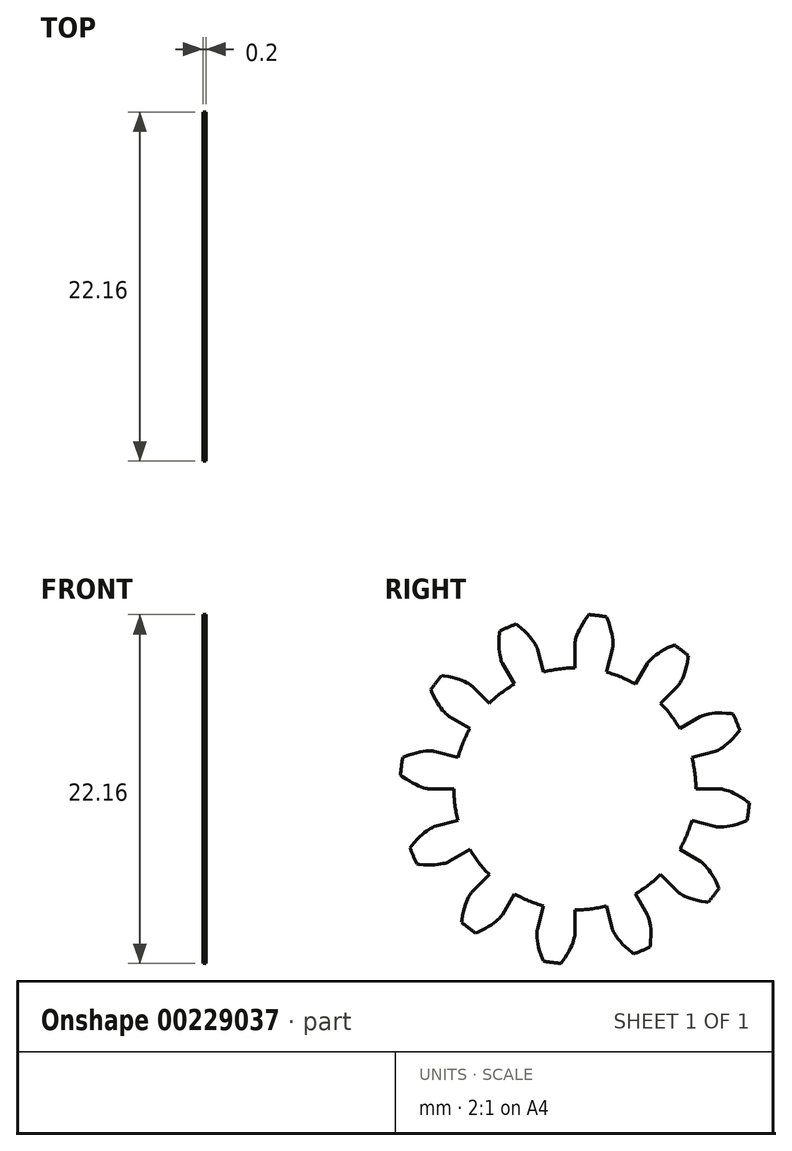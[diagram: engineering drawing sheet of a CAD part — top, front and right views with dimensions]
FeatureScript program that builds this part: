
annotation { "Feature Type Name" : "Feature", "Feature Type Description" : "" }
export const myFeature = defineFeature(function(context is Context, id is Id, definition is map)
    precondition{}
    {
        {
            assignVariable(context, id + "F0", {"name" : "GearThickness", "anyValue" : .196});
        }
        {
            var Q0;
            Q0=qCreatedBy(makeId("Right.planeOp"),FACE);
            var sketch = newSketch(context, id + "F1", { "sketchPlane" : qUnion([Q0])});
            skCircle(sketch, "E0", {"center": v(0, 0) * mm, "radius": 7.69 * mm});
            skCircle(sketch, "E1", {"center": v(0, 0) * mm, "radius": 9.22 * mm, "construction": true});
            skCircle(sketch, "E2", {"center": v(0, 0) * mm, "radius": 9.53 * mm, "construction": true});
            skCircle(sketch, "E3", {"center": v(0, 0) * mm, "radius": 11.11 * mm});
            skLineSegment(sketch, "E4", {"start": v(0, 0) * mm, "end": v(-9.22, 0) * mm, "construction": true});
            skLineSegment(sketch, "E5.1.0", {"start": v(0, 0) * mm, "end": v(-9.21, 0.46) * mm, "construction": true});
            skLineSegment(sketch, "E5.2.0", {"start": v(0, 0) * mm, "end": v(-9.18, 0.92) * mm, "construction": true});
            skLineSegment(sketch, "E5.3.0", {"start": v(0, 0) * mm, "end": v(-9.12, 1.38) * mm, "construction": true});
            skLineSegment(sketch, "E5.4.0", {"start": v(0, 0) * mm, "end": v(-9.04, 1.83) * mm, "construction": true});
            skLineSegment(sketch, "E5.5.0", {"start": v(0, 0) * mm, "end": v(-8.93, 2.28) * mm, "construction": true});
            skLineSegment(sketch, "E5.6.0", {"start": v(0, 0) * mm, "end": v(-8.8, 2.73) * mm, "construction": true});
            skLineSegment(sketch, "E5.7.0", {"start": v(0, 0) * mm, "end": v(-8.66, 3.16) * mm, "construction": true});
            skLineSegment(sketch, "E5.8.0", {"start": v(0, 0) * mm, "end": v(-8.5, 3.6) * mm, "construction": true});
            skLineSegment(sketch, "E5.9.0", {"start": v(0, 0) * mm, "end": v(-8.3, 4.01) * mm, "construction": true});
            skLineSegment(sketch, "E5.10.0", {"start": v(0, 0) * mm, "end": v(-8.1, 4.42) * mm, "construction": true});
            skLineSegment(sketch, "E5.11.0", {"start": v(0, 0) * mm, "end": v(-7.86, 4.82) * mm, "construction": true});
            skLineSegment(sketch, "E5.12.0", {"start": v(0, 0) * mm, "end": v(-7.61, 5.2) * mm, "construction": true});
            skLineSegment(sketch, "E5.13.0", {"start": v(0, 0) * mm, "end": v(-7.34, 5.58) * mm, "construction": true});
            skLineSegment(sketch, "E5.14.0", {"start": v(0, 0) * mm, "end": v(-7.05, 5.94) * mm, "construction": true});
            skLineSegment(sketch, "E5.anchor2", {"start": v(0, 0) * mm, "end": v(-7.05, 5.94) * mm, "construction": true});
            skLineSegment(sketch, "E6", {"start": v(-9.21, 0.46) * mm, "end": v(-9.23, 0) * mm, "construction": true});
            skLineSegment(sketch, "E7", {"start": v(-9.18, 0.92) * mm, "end": v(-9.27, 0) * mm, "construction": true});
            skLineSegment(sketch, "E8", {"start": v(-9.12, 1.38) * mm, "end": v(-9.32, 0.01) * mm, "construction": true});
            skLineSegment(sketch, "E9", {"start": v(-8.93, 2.28) * mm, "end": v(-9.5, 0.05) * mm, "construction": true});
            skLineSegment(sketch, "E10", {"start": v(-8.8, 2.73) * mm, "end": v(-9.63, 0.08) * mm, "construction": true});
            skLineSegment(sketch, "E11", {"start": v(-8.66, 3.16) * mm, "end": v(-9.77, 0.13) * mm, "construction": true});
            skLineSegment(sketch, "E12", {"start": v(-8.5, 3.6) * mm, "end": v(-9.93, 0.2) * mm, "construction": true});
            skLineSegment(sketch, "E13", {"start": v(-8.3, 4.01) * mm, "end": v(-10.1, 0.27) * mm, "construction": true});
            skLineSegment(sketch, "E14", {"start": v(-8.1, 4.42) * mm, "end": v(-10.3, 0.37) * mm, "construction": true});
            skLineSegment(sketch, "E15", {"start": v(-7.86, 4.82) * mm, "end": v(-10.51, 0.5) * mm, "construction": true});
            skLineSegment(sketch, "E16", {"start": v(-9.04, 1.83) * mm, "end": v(-9.4, 0.02) * mm, "construction": true});
            skLineSegment(sketch, "E17", {"start": v(-7.61, 5.2) * mm, "end": v(-10.74, 0.64) * mm, "construction": true});
            skLineSegment(sketch, "E18", {"start": v(-7.34, 5.58) * mm, "end": v(-10.97, 0.8) * mm, "construction": true});
            skLineSegment(sketch, "E19", {"start": v(-7.05, 5.94) * mm, "end": v(-11.21, 1) * mm, "construction": true});
            skLineSegment(sketch, "E20", {"start": v(0, 0) * mm, "end": v(-9.14, 1.2) * mm, "construction": true});
            skLineSegment(sketch, "E21", {"start": v(-7.69, 0) * mm, "end": v(-9.22, 0) * mm});
            skLineSegment(sketch, "E22.MirrorCS", {"start": v(-7.43, 1.99) * mm, "end": v(-8.9, 2.39) * mm});
            skLineSegment(sketch, "E23", {"start": v(-9.22, 0) * mm, "end": v(-9.23, 0) * mm});
            skLineSegment(sketch, "E24", {"start": v(-9.23, 0) * mm, "end": v(-9.27, 0) * mm});
            skLineSegment(sketch, "E25", {"start": v(-9.27, 0) * mm, "end": v(-9.32, 0.01) * mm});
            skLineSegment(sketch, "E26", {"start": v(-9.32, 0.01) * mm, "end": v(-9.4, 0.02) * mm});
            skLineSegment(sketch, "E27", {"start": v(-9.4, 0.02) * mm, "end": v(-9.5, 0.05) * mm});
            skLineSegment(sketch, "E28", {"start": v(-9.5, 0.05) * mm, "end": v(-9.63, 0.08) * mm});
            skLineSegment(sketch, "E29", {"start": v(-9.63, 0.08) * mm, "end": v(-9.77, 0.13) * mm});
            skLineSegment(sketch, "E30", {"start": v(-9.77, 0.13) * mm, "end": v(-9.93, 0.2) * mm});
            skLineSegment(sketch, "E31", {"start": v(-9.93, 0.2) * mm, "end": v(-10.1, 0.27) * mm});
            skLineSegment(sketch, "E32", {"start": v(-10.1, 0.27) * mm, "end": v(-10.3, 0.37) * mm});
            skLineSegment(sketch, "E33", {"start": v(-10.3, 0.37) * mm, "end": v(-10.51, 0.5) * mm});
            skLineSegment(sketch, "E34", {"start": v(-10.51, 0.5) * mm, "end": v(-10.74, 0.64) * mm});
            skLineSegment(sketch, "E35", {"start": v(-10.74, 0.64) * mm, "end": v(-10.97, 0.8) * mm});
            skLineSegment(sketch, "E36", {"start": v(-10.97, 0.8) * mm, "end": v(-11.21, 1) * mm});
            skLineSegment(sketch, "E37.MirrorCS", {"start": v(-8.9, 2.39) * mm, "end": v(-8.92, 2.39) * mm});
            skLineSegment(sketch, "E38.MirrorCS", {"start": v(-8.92, 2.39) * mm, "end": v(-8.95, 2.4) * mm});
            skLineSegment(sketch, "E39.MirrorCS", {"start": v(-8.95, 2.4) * mm, "end": v(-9, 2.4) * mm});
            skLineSegment(sketch, "E40.MirrorCS", {"start": v(-9, 2.4) * mm, "end": v(-9.1, 2.41) * mm});
            skLineSegment(sketch, "E41.MirrorCS", {"start": v(-9.2, 2.41) * mm, "end": v(-9.32, 2.41) * mm});
            skLineSegment(sketch, "E42.MirrorCS", {"start": v(-9.32, 2.41) * mm, "end": v(-9.47, 2.4) * mm});
            skLineSegment(sketch, "E43.MirrorCS", {"start": v(-9.47, 2.4) * mm, "end": v(-9.64, 2.38) * mm});
            skLineSegment(sketch, "E44.MirrorCS", {"start": v(-9.64, 2.38) * mm, "end": v(-9.84, 2.35) * mm});
            skLineSegment(sketch, "E45.MirrorCS", {"start": v(-10.05, 2.3) * mm, "end": v(-10.28, 2.24) * mm});
            skLineSegment(sketch, "E46.MirrorCS", {"start": v(-9.84, 2.35) * mm, "end": v(-10.05, 2.3) * mm});
            skLineSegment(sketch, "E47.MirrorCS", {"start": v(-10.28, 2.24) * mm, "end": v(-10.54, 2.16) * mm});
            skLineSegment(sketch, "E48.MirrorCS", {"start": v(-10.54, 2.16) * mm, "end": v(-10.8, 2.06) * mm});
            skLineSegment(sketch, "E49.MirrorCS", {"start": v(-10.8, 2.06) * mm, "end": v(-11.09, 1.93) * mm});
            skLineSegment(sketch, "E50.MirrorCS", {"start": v(-9.1, 2.41) * mm, "end": v(-9.2, 2.41) * mm});
            skLineSegment(sketch, "E51.1.0", {"start": v(-6.66, -3.84) * mm, "end": v(-7.99, -4.61) * mm});
            skLineSegment(sketch, "E51.1.1", {"start": v(-10.03, -3.2) * mm, "end": v(-10.2, -3.4) * mm});
            skLineSegment(sketch, "E51.1.2", {"start": v(-7.43, -1.99) * mm, "end": v(-8.9, -2.39) * mm});
            skLineSegment(sketch, "E51.1.3", {"start": v(-9.86, -3.03) * mm, "end": v(-10.03, -3.2) * mm});
            skLineSegment(sketch, "E51.1.4", {"start": v(-9.11, -4.83) * mm, "end": v(-9.35, -4.83) * mm});
            skLineSegment(sketch, "E51.1.5", {"start": v(-9.35, -4.83) * mm, "end": v(-9.62, -4.81) * mm});
            skLineSegment(sketch, "E51.1.6", {"start": v(-9.7, -2.88) * mm, "end": v(-9.86, -3.03) * mm});
            skLineSegment(sketch, "E51.1.7", {"start": v(-10.39, -3.62) * mm, "end": v(-10.57, -3.87) * mm});
            skLineSegment(sketch, "E51.1.8", {"start": v(-9.54, -2.76) * mm, "end": v(-9.7, -2.88) * mm});
            skLineSegment(sketch, "E51.1.9", {"start": v(-9.9, -4.78) * mm, "end": v(-10.21, -4.74) * mm});
            skLineSegment(sketch, "E51.1.10", {"start": v(-10.2, -3.4) * mm, "end": v(-10.39, -3.62) * mm});
            skLineSegment(sketch, "E51.1.11", {"start": v(-8.9, -4.82) * mm, "end": v(-9.11, -4.83) * mm});
            skLineSegment(sketch, "E51.1.12", {"start": v(-9.62, -4.81) * mm, "end": v(-9.9, -4.78) * mm});
            skLineSegment(sketch, "E51.1.13", {"start": v(-9.17, -2.5) * mm, "end": v(-9.28, -2.57) * mm});
            skLineSegment(sketch, "E51.1.14", {"start": v(-9.28, -2.57) * mm, "end": v(-9.4, -2.65) * mm});
            skLineSegment(sketch, "E51.1.15", {"start": v(-9.4, -2.65) * mm, "end": v(-9.54, -2.76) * mm});
            skLineSegment(sketch, "E51.1.16", {"start": v(-8.53, -4.77) * mm, "end": v(-8.7, -4.8) * mm});
            skLineSegment(sketch, "E51.1.17", {"start": v(-8.38, -4.74) * mm, "end": v(-8.53, -4.77) * mm});
            skLineSegment(sketch, "E51.1.18", {"start": v(-8.7, -4.8) * mm, "end": v(-8.9, -4.82) * mm});
            skLineSegment(sketch, "E51.1.19", {"start": v(-9.08, -2.46) * mm, "end": v(-9.17, -2.5) * mm});
            skLineSegment(sketch, "E51.1.20", {"start": v(-9, -2.42) * mm, "end": v(-9.08, -2.46) * mm});
            skLineSegment(sketch, "E51.1.21", {"start": v(-8.26, -4.71) * mm, "end": v(-8.38, -4.74) * mm});
            skLineSegment(sketch, "E51.1.22", {"start": v(-8.16, -4.68) * mm, "end": v(-8.26, -4.71) * mm});
            skLineSegment(sketch, "E51.1.23", {"start": v(-8.03, -4.63) * mm, "end": v(-8.08, -4.65) * mm});
            skLineSegment(sketch, "E51.1.24", {"start": v(-8.9, -2.39) * mm, "end": v(-8.92, -2.4) * mm});
            skLineSegment(sketch, "E51.1.25", {"start": v(-8.92, -2.4) * mm, "end": v(-8.95, -2.4) * mm});
            skLineSegment(sketch, "E51.1.26", {"start": v(-8.08, -4.65) * mm, "end": v(-8.16, -4.68) * mm});
            skLineSegment(sketch, "E51.1.27", {"start": v(-8.95, -2.4) * mm, "end": v(-9, -2.42) * mm});
            skLineSegment(sketch, "E51.1.28", {"start": v(-8, -4.62) * mm, "end": v(-8.03, -4.63) * mm});
            skLineSegment(sketch, "E51.1.29", {"start": v(-7.99, -4.61) * mm, "end": v(-8, -4.62) * mm});
            skLineSegment(sketch, "E51.2.0", {"start": v(-3.84, -6.66) * mm, "end": v(-4.61, -7.99) * mm});
            skLineSegment(sketch, "E51.2.1", {"start": v(-7.08, -7.78) * mm, "end": v(-7.14, -8.04) * mm});
            skLineSegment(sketch, "E51.2.2", {"start": v(-5.44, -5.44) * mm, "end": v(-6.52, -6.52) * mm});
            skLineSegment(sketch, "E51.2.3", {"start": v(-7.02, -7.55) * mm, "end": v(-7.08, -7.78) * mm});
            skLineSegment(sketch, "E51.2.4", {"start": v(-5.48, -8.74) * mm, "end": v(-5.69, -8.86) * mm});
            skLineSegment(sketch, "E51.2.5", {"start": v(-5.69, -8.86) * mm, "end": v(-5.92, -8.98) * mm});
            skLineSegment(sketch, "E51.2.6", {"start": v(-6.95, -7.34) * mm, "end": v(-7.02, -7.55) * mm});
            skLineSegment(sketch, "E51.2.7", {"start": v(-7.18, -8.33) * mm, "end": v(-7.22, -8.64) * mm});
            skLineSegment(sketch, "E51.2.8", {"start": v(-6.88, -7.16) * mm, "end": v(-6.95, -7.34) * mm});
            skLineSegment(sketch, "E51.2.9", {"start": v(-6.18, -9.1) * mm, "end": v(-6.47, -9.2) * mm});
            skLineSegment(sketch, "E51.2.10", {"start": v(-7.14, -8.04) * mm, "end": v(-7.18, -8.33) * mm});
            skLineSegment(sketch, "E51.2.11", {"start": v(-5.3, -8.62) * mm, "end": v(-5.48, -8.74) * mm});
            skLineSegment(sketch, "E51.2.12", {"start": v(-5.92, -8.98) * mm, "end": v(-6.18, -9.1) * mm});
            skLineSegment(sketch, "E51.2.13", {"start": v(-6.69, -6.76) * mm, "end": v(-6.75, -6.87) * mm});
            skLineSegment(sketch, "E51.2.14", {"start": v(-6.75, -6.87) * mm, "end": v(-6.82, -7) * mm});
            skLineSegment(sketch, "E51.2.15", {"start": v(-6.82, -7) * mm, "end": v(-6.88, -7.16) * mm});
            skLineSegment(sketch, "E51.2.16", {"start": v(-5, -8.4) * mm, "end": v(-5.13, -8.5) * mm});
            skLineSegment(sketch, "E51.2.17", {"start": v(-4.88, -8.3) * mm, "end": v(-5, -8.4) * mm});
            skLineSegment(sketch, "E51.2.18", {"start": v(-5.13, -8.5) * mm, "end": v(-5.3, -8.62) * mm});
            skLineSegment(sketch, "E51.2.19", {"start": v(-6.63, -6.67) * mm, "end": v(-6.69, -6.76) * mm});
            skLineSegment(sketch, "E51.2.20", {"start": v(-6.59, -6.6) * mm, "end": v(-6.63, -6.67) * mm});
            skLineSegment(sketch, "E51.2.21", {"start": v(-4.8, -8.2) * mm, "end": v(-4.88, -8.3) * mm});
            skLineSegment(sketch, "E51.2.22", {"start": v(-4.72, -8.13) * mm, "end": v(-4.8, -8.2) * mm});
            skLineSegment(sketch, "E51.2.23", {"start": v(-4.64, -8.02) * mm, "end": v(-4.67, -8.07) * mm});
            skLineSegment(sketch, "E51.2.24", {"start": v(-6.52, -6.52) * mm, "end": v(-6.53, -6.53) * mm});
            skLineSegment(sketch, "E51.2.25", {"start": v(-6.53, -6.53) * mm, "end": v(-6.55, -6.56) * mm});
            skLineSegment(sketch, "E51.2.26", {"start": v(-4.67, -8.07) * mm, "end": v(-4.72, -8.13) * mm});
            skLineSegment(sketch, "E51.2.27", {"start": v(-6.55, -6.56) * mm, "end": v(-6.59, -6.6) * mm});
            skLineSegment(sketch, "E51.2.28", {"start": v(-4.62, -8) * mm, "end": v(-4.64, -8.02) * mm});
            skLineSegment(sketch, "E51.2.29", {"start": v(-4.61, -7.99) * mm, "end": v(-4.62, -8) * mm});
            skLineSegment(sketch, "E51.3.0", {"start": v(0, -7.69) * mm, "end": v(0, -9.22) * mm});
            skLineSegment(sketch, "E51.3.1", {"start": v(-2.24, -10.28) * mm, "end": v(-2.16, -10.54) * mm});
            skLineSegment(sketch, "E51.3.2", {"start": v(-1.99, -7.43) * mm, "end": v(-2.39, -8.9) * mm});
            skLineSegment(sketch, "E51.3.3", {"start": v(-2.3, -10.05) * mm, "end": v(-2.24, -10.28) * mm});
            skLineSegment(sketch, "E51.3.4", {"start": v(-0.37, -10.3) * mm, "end": v(-0.5, -10.51) * mm});
            skLineSegment(sketch, "E51.3.5", {"start": v(-0.5, -10.51) * mm, "end": v(-0.64, -10.74) * mm});
            skLineSegment(sketch, "E51.3.6", {"start": v(-2.35, -9.84) * mm, "end": v(-2.3, -10.05) * mm});
            skLineSegment(sketch, "E51.3.7", {"start": v(-2.06, -10.8) * mm, "end": v(-1.93, -11.09) * mm});
            skLineSegment(sketch, "E51.3.8", {"start": v(-2.38, -9.64) * mm, "end": v(-2.35, -9.84) * mm});
            skLineSegment(sketch, "E51.3.9", {"start": v(-0.8, -10.97) * mm, "end": v(-1, -11.21) * mm});
            skLineSegment(sketch, "E51.3.10", {"start": v(-2.16, -10.54) * mm, "end": v(-2.06, -10.8) * mm});
            skLineSegment(sketch, "E51.3.11", {"start": v(-0.27, -10.1) * mm, "end": v(-0.37, -10.3) * mm});
            skLineSegment(sketch, "E51.3.12", {"start": v(-0.64, -10.74) * mm, "end": v(-0.8, -10.97) * mm});
            skLineSegment(sketch, "E51.3.13", {"start": v(-2.41, -9.2) * mm, "end": v(-2.41, -9.32) * mm});
            skLineSegment(sketch, "E51.3.14", {"start": v(-2.41, -9.32) * mm, "end": v(-2.4, -9.47) * mm});
            skLineSegment(sketch, "E51.3.15", {"start": v(-2.4, -9.47) * mm, "end": v(-2.38, -9.64) * mm});
            skLineSegment(sketch, "E51.3.16", {"start": v(-0.13, -9.77) * mm, "end": v(-0.2, -9.93) * mm});
            skLineSegment(sketch, "E51.3.17", {"start": v(-0.08, -9.63) * mm, "end": v(-0.13, -9.77) * mm});
            skLineSegment(sketch, "E51.3.18", {"start": v(-0.2, -9.93) * mm, "end": v(-0.27, -10.1) * mm});
            skLineSegment(sketch, "E51.3.19", {"start": v(-2.41, -9.1) * mm, "end": v(-2.41, -9.2) * mm});
            skLineSegment(sketch, "E51.3.20", {"start": v(-2.4, -9) * mm, "end": v(-2.41, -9.1) * mm});
            skLineSegment(sketch, "E51.3.21", {"start": v(-0.05, -9.5) * mm, "end": v(-0.08, -9.63) * mm});
            skLineSegment(sketch, "E51.3.22", {"start": v(-0.02, -9.4) * mm, "end": v(-0.05, -9.5) * mm});
            skLineSegment(sketch, "E51.3.23", {"start": v(0, -9.27) * mm, "end": v(-0.01, -9.32) * mm});
            skLineSegment(sketch, "E51.3.24", {"start": v(-2.39, -8.9) * mm, "end": v(-2.39, -8.92) * mm});
            skLineSegment(sketch, "E51.3.25", {"start": v(-2.39, -8.92) * mm, "end": v(-2.4, -8.95) * mm});
            skLineSegment(sketch, "E51.3.26", {"start": v(-0.01, -9.32) * mm, "end": v(-0.02, -9.4) * mm});
            skLineSegment(sketch, "E51.3.27", {"start": v(-2.4, -8.95) * mm, "end": v(-2.4, -9) * mm});
            skLineSegment(sketch, "E51.3.28", {"start": v(0, -9.23) * mm, "end": v(0, -9.27) * mm});
            skLineSegment(sketch, "E51.3.29", {"start": v(0, -9.22) * mm, "end": v(0, -9.23) * mm});
            skLineSegment(sketch, "E51.4.0", {"start": v(3.84, -6.66) * mm, "end": v(4.61, -7.99) * mm});
            skLineSegment(sketch, "E51.4.1", {"start": v(3.2, -10.03) * mm, "end": v(3.4, -10.2) * mm});
            skLineSegment(sketch, "E51.4.2", {"start": v(1.99, -7.43) * mm, "end": v(2.39, -8.9) * mm});
            skLineSegment(sketch, "E51.4.3", {"start": v(3.03, -9.86) * mm, "end": v(3.2, -10.03) * mm});
            skLineSegment(sketch, "E51.4.4", {"start": v(4.83, -9.11) * mm, "end": v(4.83, -9.35) * mm});
            skLineSegment(sketch, "E51.4.5", {"start": v(4.83, -9.35) * mm, "end": v(4.81, -9.62) * mm});
            skLineSegment(sketch, "E51.4.6", {"start": v(2.88, -9.7) * mm, "end": v(3.03, -9.86) * mm});
            skLineSegment(sketch, "E51.4.7", {"start": v(3.62, -10.39) * mm, "end": v(3.87, -10.57) * mm});
            skLineSegment(sketch, "E51.4.8", {"start": v(2.76, -9.54) * mm, "end": v(2.88, -9.7) * mm});
            skLineSegment(sketch, "E51.4.9", {"start": v(4.78, -9.9) * mm, "end": v(4.74, -10.21) * mm});
            skLineSegment(sketch, "E51.4.10", {"start": v(3.4, -10.2) * mm, "end": v(3.62, -10.39) * mm});
            skLineSegment(sketch, "E51.4.11", {"start": v(4.82, -8.9) * mm, "end": v(4.83, -9.11) * mm});
            skLineSegment(sketch, "E51.4.12", {"start": v(4.81, -9.62) * mm, "end": v(4.78, -9.9) * mm});
            skLineSegment(sketch, "E51.4.13", {"start": v(2.5, -9.17) * mm, "end": v(2.57, -9.28) * mm});
            skLineSegment(sketch, "E51.4.14", {"start": v(2.57, -9.28) * mm, "end": v(2.65, -9.4) * mm});
            skLineSegment(sketch, "E51.4.15", {"start": v(2.65, -9.4) * mm, "end": v(2.76, -9.54) * mm});
            skLineSegment(sketch, "E51.4.16", {"start": v(4.77, -8.53) * mm, "end": v(4.8, -8.7) * mm});
            skLineSegment(sketch, "E51.4.17", {"start": v(4.74, -8.38) * mm, "end": v(4.77, -8.53) * mm});
            skLineSegment(sketch, "E51.4.18", {"start": v(4.8, -8.7) * mm, "end": v(4.82, -8.9) * mm});
            skLineSegment(sketch, "E51.4.19", {"start": v(2.46, -9.08) * mm, "end": v(2.5, -9.17) * mm});
            skLineSegment(sketch, "E51.4.20", {"start": v(2.42, -9) * mm, "end": v(2.46, -9.08) * mm});
            skLineSegment(sketch, "E51.4.21", {"start": v(4.71, -8.26) * mm, "end": v(4.74, -8.38) * mm});
            skLineSegment(sketch, "E51.4.22", {"start": v(4.68, -8.16) * mm, "end": v(4.71, -8.26) * mm});
            skLineSegment(sketch, "E51.4.23", {"start": v(4.63, -8.03) * mm, "end": v(4.65, -8.08) * mm});
            skLineSegment(sketch, "E51.4.24", {"start": v(2.39, -8.9) * mm, "end": v(2.4, -8.92) * mm});
            skLineSegment(sketch, "E51.4.25", {"start": v(2.4, -8.92) * mm, "end": v(2.4, -8.95) * mm});
            skLineSegment(sketch, "E51.4.26", {"start": v(4.65, -8.08) * mm, "end": v(4.68, -8.16) * mm});
            skLineSegment(sketch, "E51.4.27", {"start": v(2.4, -8.95) * mm, "end": v(2.42, -9) * mm});
            skLineSegment(sketch, "E51.4.28", {"start": v(4.62, -8) * mm, "end": v(4.63, -8.03) * mm});
            skLineSegment(sketch, "E51.4.29", {"start": v(4.61, -7.99) * mm, "end": v(4.62, -8) * mm});
            skLineSegment(sketch, "E51.5.0", {"start": v(6.66, -3.84) * mm, "end": v(7.99, -4.61) * mm});
            skLineSegment(sketch, "E51.5.1", {"start": v(7.78, -7.08) * mm, "end": v(8.04, -7.14) * mm});
            skLineSegment(sketch, "E51.5.2", {"start": v(5.44, -5.44) * mm, "end": v(6.52, -6.52) * mm});
            skLineSegment(sketch, "E51.5.3", {"start": v(7.55, -7.02) * mm, "end": v(7.78, -7.08) * mm});
            skLineSegment(sketch, "E51.5.4", {"start": v(8.74, -5.48) * mm, "end": v(8.86, -5.69) * mm});
            skLineSegment(sketch, "E51.5.5", {"start": v(8.86, -5.69) * mm, "end": v(8.98, -5.92) * mm});
            skLineSegment(sketch, "E51.5.6", {"start": v(7.34, -6.95) * mm, "end": v(7.55, -7.02) * mm});
            skLineSegment(sketch, "E51.5.7", {"start": v(8.33, -7.18) * mm, "end": v(8.64, -7.22) * mm});
            skLineSegment(sketch, "E51.5.8", {"start": v(7.16, -6.88) * mm, "end": v(7.34, -6.95) * mm});
            skLineSegment(sketch, "E51.5.9", {"start": v(9.1, -6.18) * mm, "end": v(9.2, -6.47) * mm});
            skLineSegment(sketch, "E51.5.10", {"start": v(8.04, -7.14) * mm, "end": v(8.33, -7.18) * mm});
            skLineSegment(sketch, "E51.5.11", {"start": v(8.62, -5.3) * mm, "end": v(8.74, -5.48) * mm});
            skLineSegment(sketch, "E51.5.12", {"start": v(8.98, -5.92) * mm, "end": v(9.1, -6.18) * mm});
            skLineSegment(sketch, "E51.5.13", {"start": v(6.76, -6.69) * mm, "end": v(6.87, -6.75) * mm});
            skLineSegment(sketch, "E51.5.14", {"start": v(6.87, -6.75) * mm, "end": v(7, -6.82) * mm});
            skLineSegment(sketch, "E51.5.15", {"start": v(7, -6.82) * mm, "end": v(7.16, -6.88) * mm});
            skLineSegment(sketch, "E51.5.16", {"start": v(8.4, -5) * mm, "end": v(8.5, -5.13) * mm});
            skLineSegment(sketch, "E51.5.17", {"start": v(8.3, -4.88) * mm, "end": v(8.4, -5) * mm});
            skLineSegment(sketch, "E51.5.18", {"start": v(8.5, -5.13) * mm, "end": v(8.62, -5.3) * mm});
            skLineSegment(sketch, "E51.5.19", {"start": v(6.67, -6.63) * mm, "end": v(6.76, -6.69) * mm});
            skLineSegment(sketch, "E51.5.20", {"start": v(6.6, -6.59) * mm, "end": v(6.67, -6.63) * mm});
            skLineSegment(sketch, "E51.5.21", {"start": v(8.2, -4.8) * mm, "end": v(8.3, -4.88) * mm});
            skLineSegment(sketch, "E51.5.22", {"start": v(8.13, -4.72) * mm, "end": v(8.2, -4.8) * mm});
            skLineSegment(sketch, "E51.5.23", {"start": v(8.02, -4.64) * mm, "end": v(8.07, -4.67) * mm});
            skLineSegment(sketch, "E51.5.24", {"start": v(6.52, -6.52) * mm, "end": v(6.53, -6.53) * mm});
            skLineSegment(sketch, "E51.5.25", {"start": v(6.53, -6.53) * mm, "end": v(6.56, -6.55) * mm});
            skLineSegment(sketch, "E51.5.26", {"start": v(8.07, -4.67) * mm, "end": v(8.13, -4.72) * mm});
            skLineSegment(sketch, "E51.5.27", {"start": v(6.56, -6.55) * mm, "end": v(6.6, -6.59) * mm});
            skLineSegment(sketch, "E51.5.28", {"start": v(8, -4.62) * mm, "end": v(8.02, -4.64) * mm});
            skLineSegment(sketch, "E51.5.29", {"start": v(7.99, -4.61) * mm, "end": v(8, -4.62) * mm});
            skLineSegment(sketch, "E51.6.0", {"start": v(7.69, 0) * mm, "end": v(9.22, 0) * mm});
            skLineSegment(sketch, "E51.6.1", {"start": v(10.28, -2.24) * mm, "end": v(10.54, -2.16) * mm});
            skLineSegment(sketch, "E51.6.2", {"start": v(7.43, -1.99) * mm, "end": v(8.9, -2.39) * mm});
            skLineSegment(sketch, "E51.6.3", {"start": v(10.05, -2.3) * mm, "end": v(10.28, -2.24) * mm});
            skLineSegment(sketch, "E51.6.4", {"start": v(10.3, -0.37) * mm, "end": v(10.51, -0.5) * mm});
            skLineSegment(sketch, "E51.6.5", {"start": v(10.51, -0.5) * mm, "end": v(10.74, -0.64) * mm});
            skLineSegment(sketch, "E51.6.6", {"start": v(9.84, -2.35) * mm, "end": v(10.05, -2.3) * mm});
            skLineSegment(sketch, "E51.6.7", {"start": v(10.8, -2.06) * mm, "end": v(11.09, -1.93) * mm});
            skLineSegment(sketch, "E51.6.8", {"start": v(9.64, -2.38) * mm, "end": v(9.84, -2.35) * mm});
            skLineSegment(sketch, "E51.6.9", {"start": v(10.97, -0.8) * mm, "end": v(11.21, -1) * mm});
            skLineSegment(sketch, "E51.6.10", {"start": v(10.54, -2.16) * mm, "end": v(10.8, -2.06) * mm});
            skLineSegment(sketch, "E51.6.11", {"start": v(10.1, -0.27) * mm, "end": v(10.3, -0.37) * mm});
            skLineSegment(sketch, "E51.6.12", {"start": v(10.74, -0.64) * mm, "end": v(10.97, -0.8) * mm});
            skLineSegment(sketch, "E51.6.13", {"start": v(9.2, -2.41) * mm, "end": v(9.32, -2.41) * mm});
            skLineSegment(sketch, "E51.6.14", {"start": v(9.32, -2.41) * mm, "end": v(9.47, -2.4) * mm});
            skLineSegment(sketch, "E51.6.15", {"start": v(9.47, -2.4) * mm, "end": v(9.64, -2.38) * mm});
            skLineSegment(sketch, "E51.6.16", {"start": v(9.77, -0.13) * mm, "end": v(9.93, -0.2) * mm});
            skLineSegment(sketch, "E51.6.17", {"start": v(9.63, -0.08) * mm, "end": v(9.77, -0.13) * mm});
            skLineSegment(sketch, "E51.6.18", {"start": v(9.93, -0.2) * mm, "end": v(10.1, -0.27) * mm});
            skLineSegment(sketch, "E51.6.19", {"start": v(9.1, -2.41) * mm, "end": v(9.2, -2.41) * mm});
            skLineSegment(sketch, "E51.6.20", {"start": v(9, -2.4) * mm, "end": v(9.1, -2.41) * mm});
            skLineSegment(sketch, "E51.6.21", {"start": v(9.5, -0.05) * mm, "end": v(9.63, -0.08) * mm});
            skLineSegment(sketch, "E51.6.22", {"start": v(9.4, -0.02) * mm, "end": v(9.5, -0.05) * mm});
            skLineSegment(sketch, "E51.6.23", {"start": v(9.27, 0) * mm, "end": v(9.32, -0.01) * mm});
            skLineSegment(sketch, "E51.6.24", {"start": v(8.9, -2.39) * mm, "end": v(8.92, -2.39) * mm});
            skLineSegment(sketch, "E51.6.25", {"start": v(8.92, -2.39) * mm, "end": v(8.95, -2.4) * mm});
            skLineSegment(sketch, "E51.6.26", {"start": v(9.32, -0.01) * mm, "end": v(9.4, -0.02) * mm});
            skLineSegment(sketch, "E51.6.27", {"start": v(8.95, -2.4) * mm, "end": v(9, -2.4) * mm});
            skLineSegment(sketch, "E51.6.28", {"start": v(9.23, 0) * mm, "end": v(9.27, 0) * mm});
            skLineSegment(sketch, "E51.6.29", {"start": v(9.22, 0) * mm, "end": v(9.23, 0) * mm});
            skLineSegment(sketch, "E51.7.0", {"start": v(6.66, 3.84) * mm, "end": v(7.99, 4.61) * mm});
            skLineSegment(sketch, "E51.7.1", {"start": v(10.03, 3.2) * mm, "end": v(10.2, 3.4) * mm});
            skLineSegment(sketch, "E51.7.2", {"start": v(7.43, 1.99) * mm, "end": v(8.9, 2.39) * mm});
            skLineSegment(sketch, "E51.7.3", {"start": v(9.86, 3.03) * mm, "end": v(10.03, 3.2) * mm});
            skLineSegment(sketch, "E51.7.4", {"start": v(9.11, 4.83) * mm, "end": v(9.35, 4.83) * mm});
            skLineSegment(sketch, "E51.7.5", {"start": v(9.35, 4.83) * mm, "end": v(9.62, 4.81) * mm});
            skLineSegment(sketch, "E51.7.6", {"start": v(9.7, 2.88) * mm, "end": v(9.86, 3.03) * mm});
            skLineSegment(sketch, "E51.7.7", {"start": v(10.39, 3.62) * mm, "end": v(10.57, 3.87) * mm});
            skLineSegment(sketch, "E51.7.8", {"start": v(9.54, 2.76) * mm, "end": v(9.7, 2.88) * mm});
            skLineSegment(sketch, "E51.7.9", {"start": v(9.9, 4.78) * mm, "end": v(10.21, 4.74) * mm});
            skLineSegment(sketch, "E51.7.10", {"start": v(10.2, 3.4) * mm, "end": v(10.39, 3.62) * mm});
            skLineSegment(sketch, "E51.7.11", {"start": v(8.9, 4.82) * mm, "end": v(9.11, 4.83) * mm});
            skLineSegment(sketch, "E51.7.12", {"start": v(9.62, 4.81) * mm, "end": v(9.9, 4.78) * mm});
            skLineSegment(sketch, "E51.7.13", {"start": v(9.17, 2.5) * mm, "end": v(9.28, 2.57) * mm});
            skLineSegment(sketch, "E51.7.14", {"start": v(9.28, 2.57) * mm, "end": v(9.4, 2.65) * mm});
            skLineSegment(sketch, "E51.7.15", {"start": v(9.4, 2.65) * mm, "end": v(9.54, 2.76) * mm});
            skLineSegment(sketch, "E51.7.16", {"start": v(8.53, 4.77) * mm, "end": v(8.7, 4.8) * mm});
            skLineSegment(sketch, "E51.7.17", {"start": v(8.38, 4.74) * mm, "end": v(8.53, 4.77) * mm});
            skLineSegment(sketch, "E51.7.18", {"start": v(8.7, 4.8) * mm, "end": v(8.9, 4.82) * mm});
            skLineSegment(sketch, "E51.7.19", {"start": v(9.08, 2.46) * mm, "end": v(9.17, 2.5) * mm});
            skLineSegment(sketch, "E51.7.20", {"start": v(9, 2.42) * mm, "end": v(9.08, 2.46) * mm});
            skLineSegment(sketch, "E51.7.21", {"start": v(8.26, 4.71) * mm, "end": v(8.38, 4.74) * mm});
            skLineSegment(sketch, "E51.7.22", {"start": v(8.16, 4.68) * mm, "end": v(8.26, 4.71) * mm});
            skLineSegment(sketch, "E51.7.23", {"start": v(8.03, 4.63) * mm, "end": v(8.08, 4.65) * mm});
            skLineSegment(sketch, "E51.7.24", {"start": v(8.9, 2.39) * mm, "end": v(8.92, 2.4) * mm});
            skLineSegment(sketch, "E51.7.25", {"start": v(8.92, 2.4) * mm, "end": v(8.95, 2.4) * mm});
            skLineSegment(sketch, "E51.7.26", {"start": v(8.08, 4.65) * mm, "end": v(8.16, 4.68) * mm});
            skLineSegment(sketch, "E51.7.27", {"start": v(8.95, 2.4) * mm, "end": v(9, 2.42) * mm});
            skLineSegment(sketch, "E51.7.28", {"start": v(8, 4.62) * mm, "end": v(8.03, 4.63) * mm});
            skLineSegment(sketch, "E51.7.29", {"start": v(7.99, 4.61) * mm, "end": v(8, 4.62) * mm});
            skLineSegment(sketch, "E51.8.0", {"start": v(3.84, 6.66) * mm, "end": v(4.61, 7.99) * mm});
            skLineSegment(sketch, "E51.8.1", {"start": v(7.08, 7.78) * mm, "end": v(7.14, 8.04) * mm});
            skLineSegment(sketch, "E51.8.2", {"start": v(5.44, 5.44) * mm, "end": v(6.52, 6.52) * mm});
            skLineSegment(sketch, "E51.8.3", {"start": v(7.02, 7.55) * mm, "end": v(7.08, 7.78) * mm});
            skLineSegment(sketch, "E51.8.4", {"start": v(5.48, 8.74) * mm, "end": v(5.69, 8.86) * mm});
            skLineSegment(sketch, "E51.8.5", {"start": v(5.69, 8.86) * mm, "end": v(5.92, 8.98) * mm});
            skLineSegment(sketch, "E51.8.6", {"start": v(6.95, 7.34) * mm, "end": v(7.02, 7.55) * mm});
            skLineSegment(sketch, "E51.8.7", {"start": v(7.18, 8.33) * mm, "end": v(7.22, 8.64) * mm});
            skLineSegment(sketch, "E51.8.8", {"start": v(6.88, 7.16) * mm, "end": v(6.95, 7.34) * mm});
            skLineSegment(sketch, "E51.8.9", {"start": v(6.18, 9.1) * mm, "end": v(6.47, 9.2) * mm});
            skLineSegment(sketch, "E51.8.10", {"start": v(7.14, 8.04) * mm, "end": v(7.18, 8.33) * mm});
            skLineSegment(sketch, "E51.8.11", {"start": v(5.3, 8.62) * mm, "end": v(5.48, 8.74) * mm});
            skLineSegment(sketch, "E51.8.12", {"start": v(5.92, 8.98) * mm, "end": v(6.18, 9.1) * mm});
            skLineSegment(sketch, "E51.8.13", {"start": v(6.69, 6.76) * mm, "end": v(6.75, 6.87) * mm});
            skLineSegment(sketch, "E51.8.14", {"start": v(6.75, 6.87) * mm, "end": v(6.82, 7) * mm});
            skLineSegment(sketch, "E51.8.15", {"start": v(6.82, 7) * mm, "end": v(6.88, 7.16) * mm});
            skLineSegment(sketch, "E51.8.16", {"start": v(5, 8.4) * mm, "end": v(5.13, 8.5) * mm});
            skLineSegment(sketch, "E51.8.17", {"start": v(4.88, 8.3) * mm, "end": v(5, 8.4) * mm});
            skLineSegment(sketch, "E51.8.18", {"start": v(5.13, 8.5) * mm, "end": v(5.3, 8.62) * mm});
            skLineSegment(sketch, "E51.8.19", {"start": v(6.63, 6.67) * mm, "end": v(6.69, 6.76) * mm});
            skLineSegment(sketch, "E51.8.20", {"start": v(6.59, 6.6) * mm, "end": v(6.63, 6.67) * mm});
            skLineSegment(sketch, "E51.8.21", {"start": v(4.8, 8.2) * mm, "end": v(4.88, 8.3) * mm});
            skLineSegment(sketch, "E51.8.22", {"start": v(4.72, 8.13) * mm, "end": v(4.8, 8.2) * mm});
            skLineSegment(sketch, "E51.8.23", {"start": v(4.64, 8.02) * mm, "end": v(4.67, 8.07) * mm});
            skLineSegment(sketch, "E51.8.24", {"start": v(6.52, 6.52) * mm, "end": v(6.53, 6.53) * mm});
            skLineSegment(sketch, "E51.8.25", {"start": v(6.53, 6.53) * mm, "end": v(6.55, 6.56) * mm});
            skLineSegment(sketch, "E51.8.26", {"start": v(4.67, 8.07) * mm, "end": v(4.72, 8.13) * mm});
            skLineSegment(sketch, "E51.8.27", {"start": v(6.55, 6.56) * mm, "end": v(6.59, 6.6) * mm});
            skLineSegment(sketch, "E51.8.28", {"start": v(4.62, 8) * mm, "end": v(4.64, 8.02) * mm});
            skLineSegment(sketch, "E51.8.29", {"start": v(4.61, 7.99) * mm, "end": v(4.62, 8) * mm});
            skLineSegment(sketch, "E51.9.0", {"start": v(0, 7.69) * mm, "end": v(0, 9.22) * mm});
            skLineSegment(sketch, "E51.9.1", {"start": v(2.24, 10.28) * mm, "end": v(2.16, 10.54) * mm});
            skLineSegment(sketch, "E51.9.2", {"start": v(1.99, 7.43) * mm, "end": v(2.39, 8.9) * mm});
            skLineSegment(sketch, "E51.9.3", {"start": v(2.3, 10.05) * mm, "end": v(2.24, 10.28) * mm});
            skLineSegment(sketch, "E51.9.4", {"start": v(0.37, 10.3) * mm, "end": v(0.5, 10.51) * mm});
            skLineSegment(sketch, "E51.9.5", {"start": v(0.5, 10.51) * mm, "end": v(0.64, 10.74) * mm});
            skLineSegment(sketch, "E51.9.6", {"start": v(2.35, 9.84) * mm, "end": v(2.3, 10.05) * mm});
            skLineSegment(sketch, "E51.9.7", {"start": v(2.06, 10.8) * mm, "end": v(1.93, 11.09) * mm});
            skLineSegment(sketch, "E51.9.8", {"start": v(2.38, 9.64) * mm, "end": v(2.35, 9.84) * mm});
            skLineSegment(sketch, "E51.9.9", {"start": v(0.8, 10.97) * mm, "end": v(1, 11.21) * mm});
            skLineSegment(sketch, "E51.9.10", {"start": v(2.16, 10.54) * mm, "end": v(2.06, 10.8) * mm});
            skLineSegment(sketch, "E51.9.11", {"start": v(0.27, 10.1) * mm, "end": v(0.37, 10.3) * mm});
            skLineSegment(sketch, "E51.9.12", {"start": v(0.64, 10.74) * mm, "end": v(0.8, 10.97) * mm});
            skLineSegment(sketch, "E51.9.13", {"start": v(2.41, 9.2) * mm, "end": v(2.41, 9.32) * mm});
            skLineSegment(sketch, "E51.9.14", {"start": v(2.41, 9.32) * mm, "end": v(2.4, 9.47) * mm});
            skLineSegment(sketch, "E51.9.15", {"start": v(2.4, 9.47) * mm, "end": v(2.38, 9.64) * mm});
            skLineSegment(sketch, "E51.9.16", {"start": v(0.13, 9.77) * mm, "end": v(0.2, 9.93) * mm});
            skLineSegment(sketch, "E51.9.17", {"start": v(0.08, 9.63) * mm, "end": v(0.13, 9.77) * mm});
            skLineSegment(sketch, "E51.9.18", {"start": v(0.2, 9.93) * mm, "end": v(0.27, 10.1) * mm});
            skLineSegment(sketch, "E51.9.19", {"start": v(2.41, 9.1) * mm, "end": v(2.41, 9.2) * mm});
            skLineSegment(sketch, "E51.9.20", {"start": v(2.4, 9) * mm, "end": v(2.41, 9.1) * mm});
            skLineSegment(sketch, "E51.9.21", {"start": v(0.05, 9.5) * mm, "end": v(0.08, 9.63) * mm});
            skLineSegment(sketch, "E51.9.22", {"start": v(0.02, 9.4) * mm, "end": v(0.05, 9.5) * mm});
            skLineSegment(sketch, "E51.9.23", {"start": v(0, 9.27) * mm, "end": v(0.01, 9.32) * mm});
            skLineSegment(sketch, "E51.9.24", {"start": v(2.39, 8.9) * mm, "end": v(2.39, 8.92) * mm});
            skLineSegment(sketch, "E51.9.25", {"start": v(2.39, 8.92) * mm, "end": v(2.4, 8.95) * mm});
            skLineSegment(sketch, "E51.9.26", {"start": v(0.01, 9.32) * mm, "end": v(0.02, 9.4) * mm});
            skLineSegment(sketch, "E51.9.27", {"start": v(2.4, 8.95) * mm, "end": v(2.4, 9) * mm});
            skLineSegment(sketch, "E51.9.28", {"start": v(0, 9.23) * mm, "end": v(0, 9.27) * mm});
            skLineSegment(sketch, "E51.9.29", {"start": v(0, 9.22) * mm, "end": v(0, 9.23) * mm});
            skLineSegment(sketch, "E51.10.0", {"start": v(-3.84, 6.66) * mm, "end": v(-4.61, 7.99) * mm});
            skLineSegment(sketch, "E51.10.1", {"start": v(-3.2, 10.03) * mm, "end": v(-3.4, 10.2) * mm});
            skLineSegment(sketch, "E51.10.2", {"start": v(-1.99, 7.43) * mm, "end": v(-2.39, 8.9) * mm});
            skLineSegment(sketch, "E51.10.3", {"start": v(-3.03, 9.86) * mm, "end": v(-3.2, 10.03) * mm});
            skLineSegment(sketch, "E51.10.4", {"start": v(-4.83, 9.11) * mm, "end": v(-4.83, 9.35) * mm});
            skLineSegment(sketch, "E51.10.5", {"start": v(-4.83, 9.35) * mm, "end": v(-4.81, 9.62) * mm});
            skLineSegment(sketch, "E51.10.6", {"start": v(-2.88, 9.7) * mm, "end": v(-3.03, 9.86) * mm});
            skLineSegment(sketch, "E51.10.7", {"start": v(-3.62, 10.39) * mm, "end": v(-3.87, 10.57) * mm});
            skLineSegment(sketch, "E51.10.8", {"start": v(-2.76, 9.54) * mm, "end": v(-2.88, 9.7) * mm});
            skLineSegment(sketch, "E51.10.9", {"start": v(-4.78, 9.9) * mm, "end": v(-4.74, 10.21) * mm});
            skLineSegment(sketch, "E51.10.10", {"start": v(-3.4, 10.2) * mm, "end": v(-3.62, 10.39) * mm});
            skLineSegment(sketch, "E51.10.11", {"start": v(-4.82, 8.9) * mm, "end": v(-4.83, 9.11) * mm});
            skLineSegment(sketch, "E51.10.12", {"start": v(-4.81, 9.62) * mm, "end": v(-4.78, 9.9) * mm});
            skLineSegment(sketch, "E51.10.13", {"start": v(-2.5, 9.17) * mm, "end": v(-2.57, 9.28) * mm});
            skLineSegment(sketch, "E51.10.14", {"start": v(-2.57, 9.28) * mm, "end": v(-2.65, 9.4) * mm});
            skLineSegment(sketch, "E51.10.15", {"start": v(-2.65, 9.4) * mm, "end": v(-2.76, 9.54) * mm});
            skLineSegment(sketch, "E51.10.16", {"start": v(-4.77, 8.53) * mm, "end": v(-4.8, 8.7) * mm});
            skLineSegment(sketch, "E51.10.17", {"start": v(-4.74, 8.38) * mm, "end": v(-4.77, 8.53) * mm});
            skLineSegment(sketch, "E51.10.18", {"start": v(-4.8, 8.7) * mm, "end": v(-4.82, 8.9) * mm});
            skLineSegment(sketch, "E51.10.19", {"start": v(-2.46, 9.08) * mm, "end": v(-2.5, 9.17) * mm});
            skLineSegment(sketch, "E51.10.20", {"start": v(-2.42, 9) * mm, "end": v(-2.46, 9.08) * mm});
            skLineSegment(sketch, "E51.10.21", {"start": v(-4.71, 8.26) * mm, "end": v(-4.74, 8.38) * mm});
            skLineSegment(sketch, "E51.10.22", {"start": v(-4.68, 8.16) * mm, "end": v(-4.71, 8.26) * mm});
            skLineSegment(sketch, "E51.10.23", {"start": v(-4.63, 8.03) * mm, "end": v(-4.65, 8.08) * mm});
            skLineSegment(sketch, "E51.10.24", {"start": v(-2.39, 8.9) * mm, "end": v(-2.4, 8.92) * mm});
            skLineSegment(sketch, "E51.10.25", {"start": v(-2.4, 8.92) * mm, "end": v(-2.4, 8.95) * mm});
            skLineSegment(sketch, "E51.10.26", {"start": v(-4.65, 8.08) * mm, "end": v(-4.68, 8.16) * mm});
            skLineSegment(sketch, "E51.10.27", {"start": v(-2.4, 8.95) * mm, "end": v(-2.42, 9) * mm});
            skLineSegment(sketch, "E51.10.28", {"start": v(-4.62, 8) * mm, "end": v(-4.63, 8.03) * mm});
            skLineSegment(sketch, "E51.10.29", {"start": v(-4.61, 7.99) * mm, "end": v(-4.62, 8) * mm});
            skLineSegment(sketch, "E51.11.0", {"start": v(-6.66, 3.84) * mm, "end": v(-7.99, 4.61) * mm});
            skLineSegment(sketch, "E51.11.1", {"start": v(-7.78, 7.08) * mm, "end": v(-8.04, 7.14) * mm});
            skLineSegment(sketch, "E51.11.2", {"start": v(-5.44, 5.44) * mm, "end": v(-6.52, 6.52) * mm});
            skLineSegment(sketch, "E51.11.3", {"start": v(-7.55, 7.02) * mm, "end": v(-7.78, 7.08) * mm});
            skLineSegment(sketch, "E51.11.4", {"start": v(-8.74, 5.48) * mm, "end": v(-8.86, 5.69) * mm});
            skLineSegment(sketch, "E51.11.5", {"start": v(-8.86, 5.69) * mm, "end": v(-8.98, 5.92) * mm});
            skLineSegment(sketch, "E51.11.6", {"start": v(-7.34, 6.95) * mm, "end": v(-7.55, 7.02) * mm});
            skLineSegment(sketch, "E51.11.7", {"start": v(-8.33, 7.18) * mm, "end": v(-8.64, 7.22) * mm});
            skLineSegment(sketch, "E51.11.8", {"start": v(-7.16, 6.88) * mm, "end": v(-7.34, 6.95) * mm});
            skLineSegment(sketch, "E51.11.9", {"start": v(-9.1, 6.18) * mm, "end": v(-9.2, 6.47) * mm});
            skLineSegment(sketch, "E51.11.10", {"start": v(-8.04, 7.14) * mm, "end": v(-8.33, 7.18) * mm});
            skLineSegment(sketch, "E51.11.11", {"start": v(-8.62, 5.3) * mm, "end": v(-8.74, 5.48) * mm});
            skLineSegment(sketch, "E51.11.12", {"start": v(-8.98, 5.92) * mm, "end": v(-9.1, 6.18) * mm});
            skLineSegment(sketch, "E51.11.13", {"start": v(-6.76, 6.69) * mm, "end": v(-6.87, 6.75) * mm});
            skLineSegment(sketch, "E51.11.14", {"start": v(-6.87, 6.75) * mm, "end": v(-7, 6.82) * mm});
            skLineSegment(sketch, "E51.11.15", {"start": v(-7, 6.82) * mm, "end": v(-7.16, 6.88) * mm});
            skLineSegment(sketch, "E51.11.16", {"start": v(-8.4, 5) * mm, "end": v(-8.5, 5.13) * mm});
            skLineSegment(sketch, "E51.11.17", {"start": v(-8.3, 4.88) * mm, "end": v(-8.4, 5) * mm});
            skLineSegment(sketch, "E51.11.18", {"start": v(-8.5, 5.13) * mm, "end": v(-8.62, 5.3) * mm});
            skLineSegment(sketch, "E51.11.19", {"start": v(-6.67, 6.63) * mm, "end": v(-6.76, 6.69) * mm});
            skLineSegment(sketch, "E51.11.20", {"start": v(-6.6, 6.59) * mm, "end": v(-6.67, 6.63) * mm});
            skLineSegment(sketch, "E51.11.21", {"start": v(-8.2, 4.8) * mm, "end": v(-8.3, 4.88) * mm});
            skLineSegment(sketch, "E51.11.22", {"start": v(-8.13, 4.72) * mm, "end": v(-8.2, 4.8) * mm});
            skLineSegment(sketch, "E51.11.23", {"start": v(-8.02, 4.64) * mm, "end": v(-8.07, 4.67) * mm});
            skLineSegment(sketch, "E51.11.24", {"start": v(-6.52, 6.52) * mm, "end": v(-6.53, 6.53) * mm});
            skLineSegment(sketch, "E51.11.25", {"start": v(-6.53, 6.53) * mm, "end": v(-6.56, 6.55) * mm});
            skLineSegment(sketch, "E51.11.26", {"start": v(-8.07, 4.67) * mm, "end": v(-8.13, 4.72) * mm});
            skLineSegment(sketch, "E51.11.27", {"start": v(-6.56, 6.55) * mm, "end": v(-6.6, 6.59) * mm});
            skLineSegment(sketch, "E51.11.28", {"start": v(-8, 4.62) * mm, "end": v(-8.02, 4.64) * mm});
            skLineSegment(sketch, "E51.11.29", {"start": v(-7.99, 4.61) * mm, "end": v(-8, 4.62) * mm});
            skSolve(sketch);
        }
        {
            var Q0;
            {var subQ0=sQuery(id+"F1.wireOp",EDGE,"E0");var subQ27=makeQuery(id+"F1.imprint","INTERSECT",VERTEX,{"derivedFrom":[subQ0,sQuery(id+"F1.wireOp",EDGE,"E51.10.0")]});Q0=makeQuery(id+"F1.imprint","IMPRINT",FACE,{"disambiguationData":[TD([[makeQuery(id+"F1.imprint","IMPRINT",EDGE,{"disambiguationData":[TD([[subQ27,-1.0]])],"derivedFrom":subQ0}),1.0]])]});}
            var Q1;
            {var subQ0=sQuery(id+"F1.wireOp",EDGE,"E51.1.0");Q1=makeQuery(id+"F1.imprint","IMPRINT",FACE,{"disambiguationData":[TD([[makeQuery(id+"F1.imprint","IMPRINT",EDGE,{"derivedFrom":subQ0}),-1.0]])]});}
            var Q2;
            {var subQ7=sQuery(id+"F1.wireOp",EDGE,"E51.2.0");Q2=makeQuery(id+"F1.imprint","IMPRINT",FACE,{"disambiguationData":[TD([[makeQuery(id+"F1.imprint","IMPRINT",EDGE,{"derivedFrom":subQ7}),-1.0]])]});}
            var Q3;
            {var subQ8=sQuery(id+"F1.wireOp",EDGE,"E51.3.0");Q3=makeQuery(id+"F1.imprint","IMPRINT",FACE,{"disambiguationData":[TD([[makeQuery(id+"F1.imprint","IMPRINT",EDGE,{"derivedFrom":subQ8}),-1.0]])]});}
            var Q4;
            {var subQ2=sQuery(id+"F1.wireOp",EDGE,"E51.4.0");Q4=makeQuery(id+"F1.imprint","IMPRINT",FACE,{"disambiguationData":[TD([[makeQuery(id+"F1.imprint","IMPRINT",EDGE,{"derivedFrom":subQ2}),-1.0]])]});}
            var Q5;
            {var subQ8=sQuery(id+"F1.wireOp",EDGE,"E51.5.0");Q5=makeQuery(id+"F1.imprint","IMPRINT",FACE,{"disambiguationData":[TD([[makeQuery(id+"F1.imprint","IMPRINT",EDGE,{"derivedFrom":subQ8}),-1.0]])]});}
            var Q6;
            {var subQ3=sQuery(id+"F1.wireOp",EDGE,"E51.6.0");Q6=makeQuery(id+"F1.imprint","IMPRINT",FACE,{"disambiguationData":[TD([[makeQuery(id+"F1.imprint","IMPRINT",EDGE,{"derivedFrom":subQ3}),-1.0]])]});}
            var Q7;
            {var subQ0=sQuery(id+"F1.wireOp",EDGE,"E51.7.0");Q7=makeQuery(id+"F1.imprint","IMPRINT",FACE,{"disambiguationData":[TD([[makeQuery(id+"F1.imprint","IMPRINT",EDGE,{"derivedFrom":subQ0}),-1.0]])]});}
            var Q8;
            {var subQ5=sQuery(id+"F1.wireOp",EDGE,"E51.8.0");Q8=makeQuery(id+"F1.imprint","IMPRINT",FACE,{"disambiguationData":[TD([[makeQuery(id+"F1.imprint","IMPRINT",EDGE,{"derivedFrom":subQ5}),-1.0]])]});}
            var Q9;
            {var subQ1=sQuery(id+"F1.wireOp",EDGE,"E51.9.0");Q9=makeQuery(id+"F1.imprint","IMPRINT",FACE,{"disambiguationData":[TD([[makeQuery(id+"F1.imprint","IMPRINT",EDGE,{"derivedFrom":subQ1}),-1.0]])]});}
            var Q10;
            {var subQ5=sQuery(id+"F1.wireOp",EDGE,"E51.10.0");Q10=makeQuery(id+"F1.imprint","IMPRINT",FACE,{"disambiguationData":[TD([[makeQuery(id+"F1.imprint","IMPRINT",EDGE,{"derivedFrom":subQ5}),-1.0]])]});}
            var Q11;
            {var subQ8=sQuery(id+"F1.wireOp",EDGE,"E51.11.0");Q11=makeQuery(id+"F1.imprint","IMPRINT",FACE,{"disambiguationData":[TD([[makeQuery(id+"F1.imprint","IMPRINT",EDGE,{"derivedFrom":subQ8}),-1.0]])]});}
            var Q12;
            {var subQ2=sQuery(id+"F1.wireOp",EDGE,"E51.12.0");Q12=makeQuery(id+"F1.imprint","IMPRINT",FACE,{"disambiguationData":[TD([[makeQuery(id+"F1.imprint","IMPRINT",EDGE,{"derivedFrom":subQ2}),-1.0]])]});}
            var Q13;
            {var subQ3=sQuery(id+"F1.wireOp",EDGE,"E51.13.0");Q13=makeQuery(id+"F1.imprint","IMPRINT",FACE,{"disambiguationData":[TD([[makeQuery(id+"F1.imprint","IMPRINT",EDGE,{"derivedFrom":subQ3}),-1.0]])]});}
            var Q14;
            {var subQ0=sQuery(id+"F1.wireOp",EDGE,"E51.14.0");Q14=makeQuery(id+"F1.imprint","IMPRINT",FACE,{"disambiguationData":[TD([[makeQuery(id+"F1.imprint","IMPRINT",EDGE,{"derivedFrom":subQ0}),-1.0]])]});}
            var Q15;
            {var subQ6=sQuery(id+"F1.wireOp",EDGE,"E51.15.0");Q15=makeQuery(id+"F1.imprint","IMPRINT",FACE,{"disambiguationData":[TD([[makeQuery(id+"F1.imprint","IMPRINT",EDGE,{"derivedFrom":subQ6}),-1.0]])]});}
            var Q16;
            {var subQ5=sQuery(id+"F1.wireOp",EDGE,"E51.16.0");Q16=makeQuery(id+"F1.imprint","IMPRINT",FACE,{"disambiguationData":[TD([[makeQuery(id+"F1.imprint","IMPRINT",EDGE,{"derivedFrom":subQ5}),-1.0]])]});}
            var Q17;
            {var subQ7=sQuery(id+"F1.wireOp",EDGE,"E51.17.0");Q17=makeQuery(id+"F1.imprint","IMPRINT",FACE,{"disambiguationData":[TD([[makeQuery(id+"F1.imprint","IMPRINT",EDGE,{"derivedFrom":subQ7}),-1.0]])]});}
            var Q18;
            {var subQ5=sQuery(id+"F1.wireOp",EDGE,"E51.18.0");Q18=makeQuery(id+"F1.imprint","IMPRINT",FACE,{"disambiguationData":[TD([[makeQuery(id+"F1.imprint","IMPRINT",EDGE,{"derivedFrom":subQ5}),-1.0]])]});}
            var Q19;
            {var subQ8=sQuery(id+"F1.wireOp",EDGE,"E51.19.0");Q19=makeQuery(id+"F1.imprint","IMPRINT",FACE,{"disambiguationData":[TD([[makeQuery(id+"F1.imprint","IMPRINT",EDGE,{"derivedFrom":subQ8}),-1.0]])]});}
            var Q20;
            {var subQ8=sQuery(id+"F1.wireOp",EDGE,"E21");Q20=makeQuery(id+"F1.imprint","IMPRINT",FACE,{"disambiguationData":[TD([[makeQuery(id+"F1.imprint","IMPRINT",EDGE,{"derivedFrom":subQ8}),-1.0]])]});}
            extrude(context, id + "F2", {"entities" : qUnion([Q0, Q1, Q2, Q3, Q4, Q5, Q6, Q7, Q8, Q9, Q10, Q11, Q12, Q13, Q14, Q15, Q16, Q17, Q18, Q19, Q20]), "depth" : (getVariable(context, 'GearThickness')) * mm});
        }
    });
